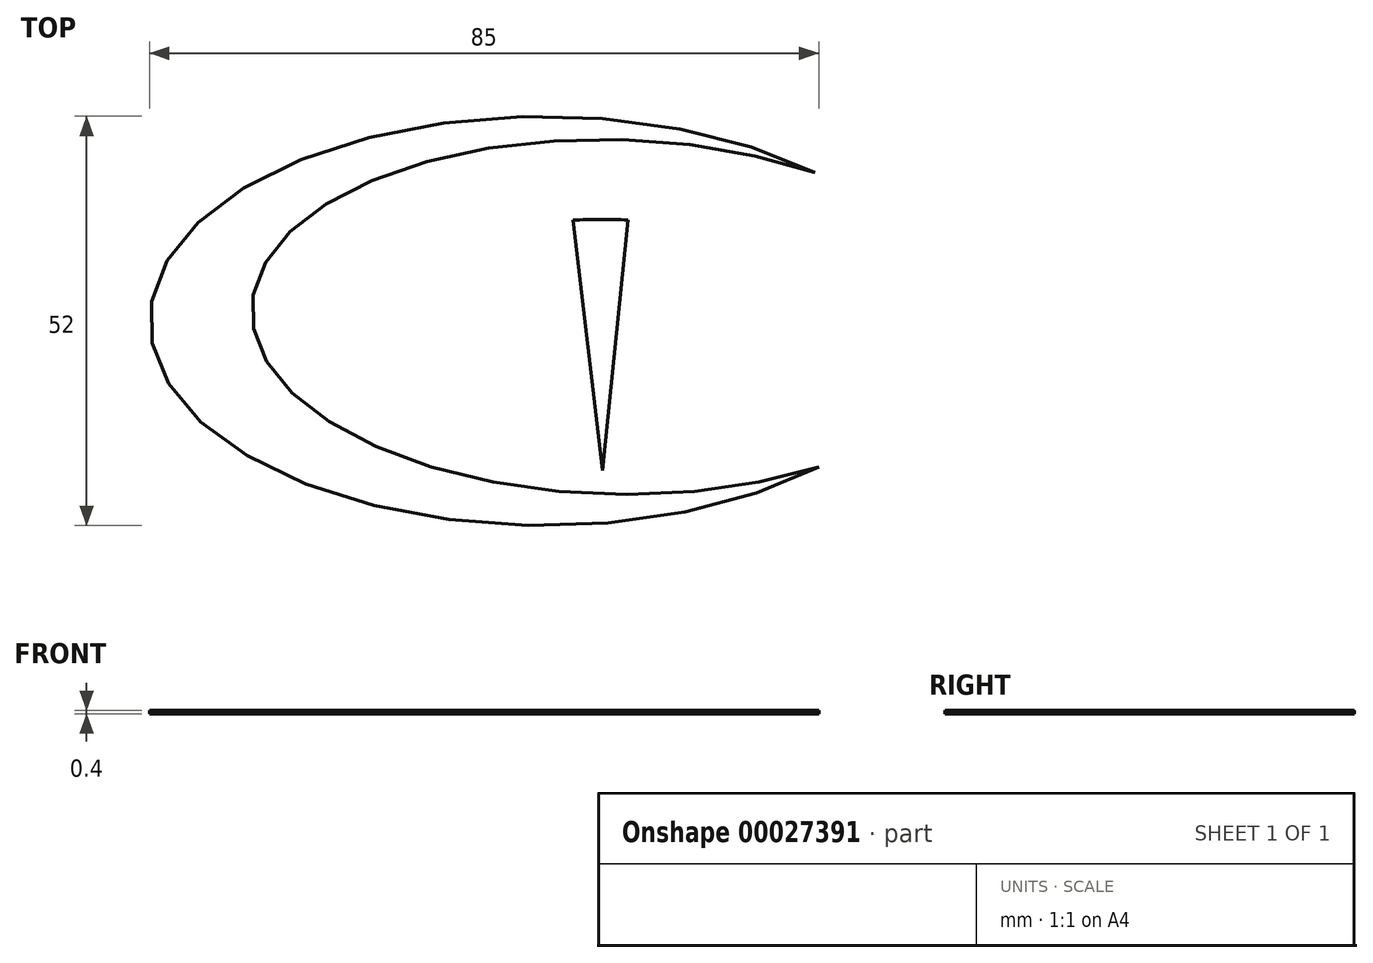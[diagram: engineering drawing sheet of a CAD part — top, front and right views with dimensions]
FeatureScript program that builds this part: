
annotation { "Feature Type Name" : "Feature", "Feature Type Description" : "" }
export const myFeature = defineFeature(function(context is Context, id is Id, definition is map)
    precondition{}
    {
        {
            var Q0;
            Q0=qCreatedBy(makeId("Top.planeOp"),FACE);
            var sketch = newSketch(context, id + "F0", { "sketchPlane" : qUnion([Q0])});
            skLineSegment(sketch, "E0", {"start": v(0, 0) * mm, "end": v(-50, 0) * mm, "construction": true});
            skLineSegment(sketch, "E1", {"start": v(0, 0) * mm, "end": v(50, 0) * mm, "construction": true});
            skLineSegment(sketch, "E2", {"start": v(0, 0) * mm, "end": v(0, 26) * mm, "construction": true});
            skEllipticalArc(sketch, "E3", {});
            skLineSegment(sketch, "E4", {"start": v(0, 0) * mm, "end": v(7.5, 0) * mm, "construction": true});
            skLineSegment(sketch, "E5", {"start": v(0, 0) * mm, "end": v(35, 0) * mm, "construction": true});
            skLineSegment(sketch, "E6", {"start": v(35, 0) * mm, "end": v(35, 17.8) * mm, "construction": true});
            skLineSegment(sketch, "E7", {"start": v(35, 0) * mm, "end": v(35, -18.57) * mm, "construction": true});
            skLineSegment(sketch, "E8", {"start": v(7.5, 0) * mm, "end": v(-35.5, 0) * mm, "construction": true});
            skLineSegment(sketch, "E9", {"start": v(0, 0) * mm, "end": v(-28.5, 0) * mm, "construction": true});
            skLineSegment(sketch, "E10", {"start": v(0, 0) * mm, "end": v(0, 19) * mm, "construction": true});
            skLineSegment(sketch, "E11", {"start": v(7.5, 0) * mm, "end": v(7.5, 19) * mm, "construction": true});
            skLineSegment(sketch, "E12", {"start": v(7.5, 0) * mm, "end": v(7.5, -2.5) * mm, "construction": true});
            skLineSegment(sketch, "E13", {"start": v(7.5, -2.5) * mm, "end": v(-28.5, -2.5) * mm, "construction": true});
            skLineSegment(sketch, "E14", {"start": v(-28.5, -2.5) * mm, "end": v(-28.5, 0) * mm, "construction": true});
            skLineSegment(sketch, "E15", {"start": v(7.5, 19) * mm, "end": v(7.5, 15) * mm, "construction": true});
            skLineSegment(sketch, "E16", {"start": v(-28.5, -2.5) * mm, "end": v(-24.5, -2.5) * mm, "construction": true});
            skLineSegment(sketch, "E17", {"start": v(3.75, 0) * mm, "end": v(3.75, 12.78) * mm, "construction": true});
            skLineSegment(sketch, "E18", {"start": v(3.75, 0) * mm, "end": v(10.75, 0) * mm, "construction": true});
            skLineSegment(sketch, "E19", {"start": v(10.75, 0) * mm, "end": v(10.75, 12.8) * mm, "construction": true});
            skLineSegment(sketch, "E20", {"start": v(7.5, 0) * mm, "end": v(7.5, 1) * mm, "construction": true});
            skEllipticalArc(sketch, "E21", {});
            skLineSegment(sketch, "E22", {"start": v(7.5, 19) * mm, "end": v(7.5, -19) * mm, "construction": true});
            skLineSegment(sketch, "E23", {"start": v(0, 0) * mm, "end": v(0, 0.5) * mm, "construction": true});
            skLineSegment(sketch, "E24", {"start": v(0, 0.5) * mm, "end": v(9, 0.5) * mm, "construction": true});
            skLineSegment(sketch, "E25", {"start": v(-35.5, 0) * mm, "end": v(-35.49, 0.5) * mm, "construction": true});
            skLineSegment(sketch, "E26", {"start": v(10.75, 0) * mm, "end": v(10.75, 23) * mm, "construction": true});
            skEllipticalArc(sketch, "E27", {});
            skEllipticalArc(sketch, "E28", {});
            skEllipticalArc(sketch, "E29", {});
            skLineSegment(sketch, "E30", {"start": v(3.75, 12.78) * mm, "end": v(7.5, -19) * mm});
            skLineSegment(sketch, "E31", {"start": v(10.75, 12.8) * mm, "end": v(7.5, -19) * mm});
            const initialGuessF0  = {"E3": [0, 0, 1, 0, 0.05, 0.026, 0.8095121727344234, 5.487786476995443], "E21": [0.0075, 0.001, 0, 1, 0.018, 0.03605568448803779, 4.094150160993872, 2.189035146185713], "E27": [0.009, 0.0005, -0.9997283167440305, 0.02330864003213095, 0.046044621626865026, 0.0225426576197948, 4.136925323083973, 2.1823847201364033], "E28": [0.0075, -0.0025, -1, 0, 0.032, 0.0153893750178721, 2.519429826364226, 0.6221628272255667], "E29": [0.0075, 0.001, 0, 1, 0.018, 0.03605568448803779, 3.9471447708338965, 2.3360405363456898]};
            skSetInitialGuess(sketch, initialGuessF0);
            skSolve(sketch);
        }
        {
            var Q0;
            Q0=makeQuery(id+"F0.imprint","IMPRINT",FACE,{"disambiguationData":[TD([[makeQuery(id+"F0.imprint","IMPRINT",EDGE,{"derivedFrom":sQuery(id+"F0.wireOp",EDGE,"E3")}),1.0]])]});
            var Q1;
            {var subQ0=sQuery(id+"F0.wireOp",EDGE,"E29");var subQ1=makeQuery(id+"F0.imprint","IMPRINT",VERTEX,{"derivedFrom":subQ0});Q1=makeQuery(id+"F0.imprint","IMPRINT",FACE,{"disambiguationData":[TD([[makeQuery(id+"F0.imprint","IMPRINT",EDGE,{"disambiguationData":[TD([[subQ1,-1.0]])],"derivedFrom":subQ0}),1.0]])]});}
            var Q2;
            {var subQ1=sQuery(id+"F0.wireOp",EDGE,"E30");Q2=makeQuery(id+"F0.imprint","IMPRINT",FACE,{"disambiguationData":[TD([[makeQuery(id+"F0.imprint","IMPRINT",EDGE,{"derivedFrom":subQ1}),1.0]])]});}
            extrude(context, id + "F1", {"entities" : qUnion([Q0, Q1, Q2]), "depth" : .4 * mm});
        }
    });
